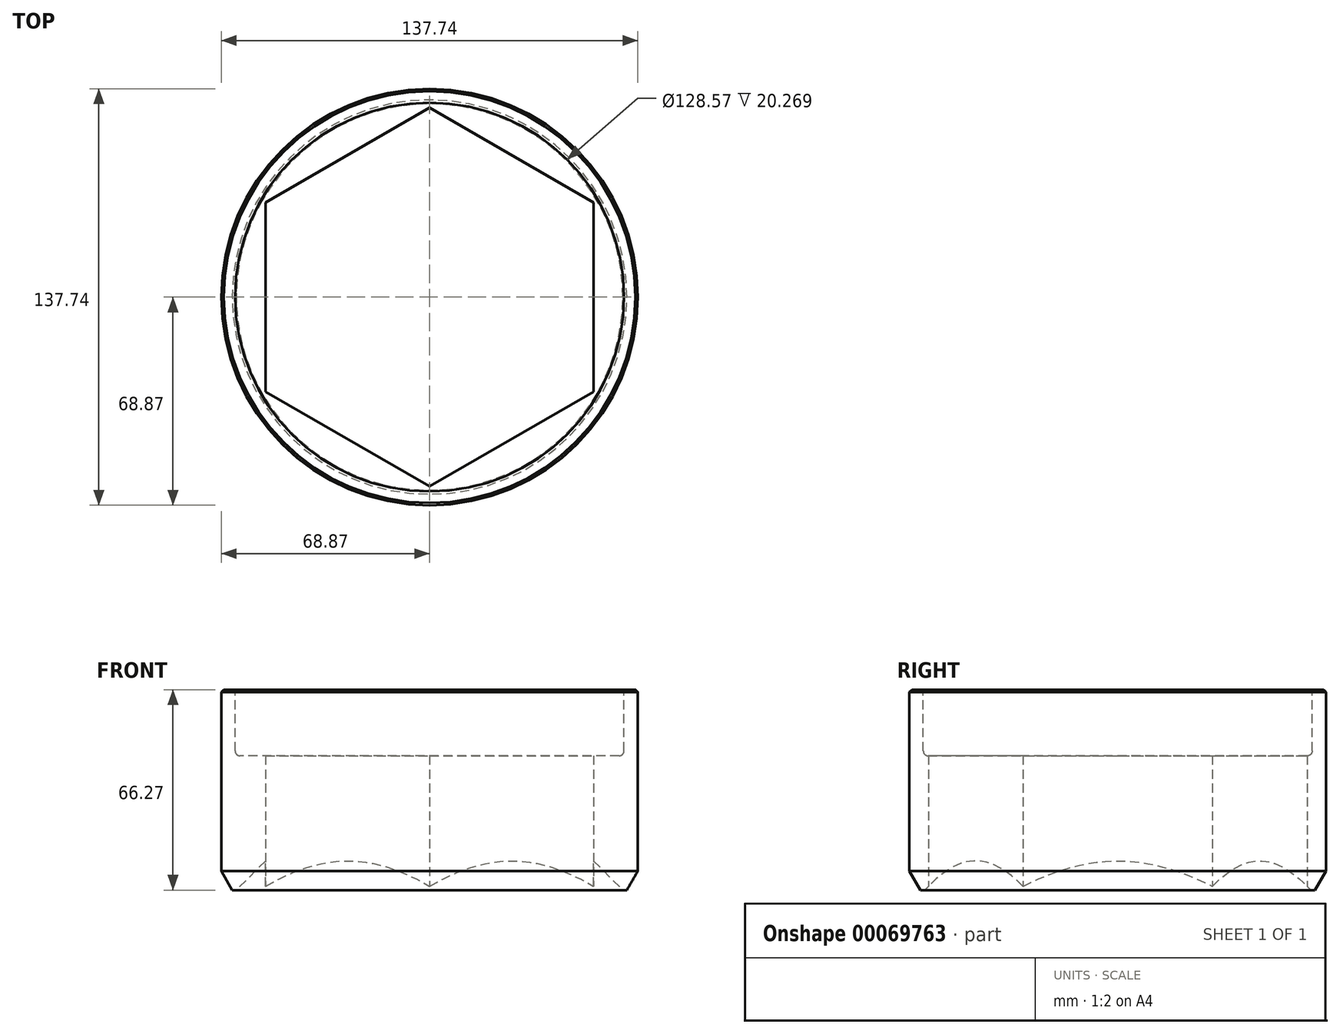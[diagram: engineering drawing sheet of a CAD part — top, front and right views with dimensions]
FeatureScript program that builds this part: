
annotation { "Feature Type Name" : "Feature", "Feature Type Description" : "" }
export const myFeature = defineFeature(function(context is Context, id is Id, definition is map)
    precondition{}
    {
        {
            var Q0;
            Q0=qCreatedBy(makeId("Right.planeOp"),FACE);
            var sketch = newSketch(context, id + "F0", { "sketchPlane" : qUnion([Q0])});
            skLineSegment(sketch, "E0", {"start": v(0, 0) * mm, "end": v(0, -66.27) * mm, "construction": true});
            skLineSegment(sketch, "E1.0", {"start": v(68.87, 0) * mm, "end": v(68.87, -66.27) * mm});
            skLineSegment(sketch, "E2.0", {"start": v(54.23, 0) * mm, "end": v(54.23, -66.27) * mm});
            skLineSegment(sketch, "E3", {"start": v(54.23, 0) * mm, "end": v(68.87, 0) * mm});
            skLineSegment(sketch, "E4", {"start": v(54.23, -66.27) * mm, "end": v(68.87, -66.27) * mm});
            skSolve(sketch);
        }
        {
            var Q0;
            Q0 = qSketchRegion(id + "F0", true);
            var Q1;
            Q1=sQuery(id+"F0.wireOp",EDGE,"E0");
            revolve(context, id + "F1", {"entities" : qUnion([Q0]), "axis" : qUnion([Q1]), "revolveType" : RevolveType.FULL});
        }
        {
            var Q0;
            Q0=makeQuery(id+"F1.opRevolve","SWEPT_FACE",FACE,{"disambiguationData":[OSD([sQuery(id+"F0.wireOp",EDGE,"E3")])]});
            var sketch = newSketch(context, id + "F2", { "sketchPlane" : qUnion([Q0])});
            skCircle(sketch, "E5", {"center": v(0, 0) * mm, "radius": 64.29 * mm});
            skSolve(sketch);
        }
        {
            var Q0;
            Q0 = qSketchRegion(id + "F2", true);
            extrude(context, id + "F3", {"entities" : qUnion([Q0]), "operationType" : NewBodyOperationType.REMOVE, "oppositeDirection" : true, "depth" : 21.84 * mm});
        }
        {
            var Q0;
            Q0=makeQuery(id+"F1.opRevolve","SWEPT_FACE",FACE,{"disambiguationData":[OSD([sQuery(id+"F0.wireOp",EDGE,"E4")])]});
            var sketch = newSketch(context, id + "F4", { "sketchPlane" : qUnion([Q0])});
            skCircle(sketch, "E6.cCircle", {"center": v(0, 0) * mm, "radius": 54.23 * mm, "construction": true});
            skLineSegment(sketch, "E6.0", {"start": v(-54.23, -31.3) * mm, "end": v(-54.23, 31.3) * mm});
            skLineSegment(sketch, "E6.1", {"start": v(-54.23, 31.3) * mm, "end": v(0, 62.62) * mm});
            skLineSegment(sketch, "E6.2", {"start": v(0, 62.62) * mm, "end": v(54.23, 31.3) * mm});
            skLineSegment(sketch, "E6.3", {"start": v(54.23, 31.3) * mm, "end": v(54.23, -31.3) * mm});
            skLineSegment(sketch, "E6.4", {"start": v(54.23, -31.3) * mm, "end": v(0, -62.62) * mm});
            skLineSegment(sketch, "E6.5", {"start": v(0, -62.62) * mm, "end": v(-54.23, -31.3) * mm});
            skPoint(sketch, "E6.0.midPoint", {"position": v(-54.23, 0) * mm});
            skSolve(sketch);
        }
        {
            var Q0;
            Q0 = qSketchRegion(id + "F4", true);
            extrude(context, id + "F5", {"entities" : qUnion([Q0]), "operationType" : NewBodyOperationType.REMOVE, "endBound" : BoundingType.THROUGH_ALL, "oppositeDirection" : true, "depth" : 25.4 * mm});
        }
        {
            var Q0;
            Q0=makeQuery(id+"F3.boolean.opBoolean","COPY",EDGE,{"derivedFrom":makeQuery(id+"F3.opExtrude","CAP_EDGE",EDGE,{"disambiguationData":[OSD([sQuery(id+"F2.wireOp",EDGE,"E5")])],"isStart":false})});
            fillet(context, id + "F6", {"entities" : qUnion([Q0]), "radius" : 1.57 * mm, "tangentPropagation" : true, "allowEdgeOverflow" : false});
        }
        {
            var Q0;
            Q0=makeQuery(id+"F1.opRevolve","SWEPT_EDGE",EDGE,{"disambiguationData":[OSD([sQuery(id+"F0.wireOp",EDGE,"E1.0"),sQuery(id+"F0.wireOp",EDGE,"E3")])]});
            var Q1;
            Q1=makeQuery(id+"F3.boolean.opBoolean","COPY",EDGE,{"derivedFrom":makeQuery(id+"F3.opExtrude","CAP_EDGE",EDGE,{"disambiguationData":[OSD([sQuery(id+"F2.wireOp",EDGE,"E5")])],"isStart":true})});
            chamfer(context, id + "F7", {"entities" : qUnion([Q0, Q1]), "width" : 0.79 * mm, "tangentPropagation" : true});
        }
        {
            var Q0;
            Q0=qCreatedBy(makeId("Right.planeOp"),FACE);
            var sketch = newSketch(context, id + "F8", { "sketchPlane" : qUnion([Q0])});
            skLineSegment(sketch, "E7.0", {"start": v(-63.9, -66.27) * mm, "end": v(0, -66.27) * mm});
            skLineSegment(sketch, "E8", {"start": v(0, -66.27) * mm, "end": v(0, -2.37) * mm});
            skLineSegment(sketch, "E9", {"start": v(-63.9, -66.27) * mm, "end": v(0, -2.37) * mm});
            skPoint(sketch, "E10.orphan", {"position": v(-68.87, -66.27) * mm});
            skPoint(sketch, "E11.orphan", {"position": v(68.87, -66.27) * mm});
            skSolve(sketch);
        }
        {
            var Q0;
            Q0 = qSketchRegion(id + "F8", true);
            var Q1;
            Q1=sQuery(id+"F8.wireOp",EDGE,"E8");
            revolve(context, id + "F9", {"operationType" : NewBodyOperationType.REMOVE, "entities" : qUnion([Q0]), "axis" : qUnion([Q1]), "revolveType" : RevolveType.FULL, "oppositeDirection" : true});
        }
        {
            var Q0;
            Q0=makeQuery(id+"F1.opRevolve","SWEPT_EDGE",EDGE,{"disambiguationData":[OSD([sQuery(id+"F0.wireOp",EDGE,"E1.0"),sQuery(id+"F0.wireOp",EDGE,"E4")])]});
            chamfer(context, id + "F10", {"entities" : qUnion([Q0]), "chamferType" : ChamferType.OFFSET_ANGLE, "width" : 6.32 * mm, "oppositeDirection" : false, "angle" : 30 * degree, "tangentPropagation" : true});
        }
    });
